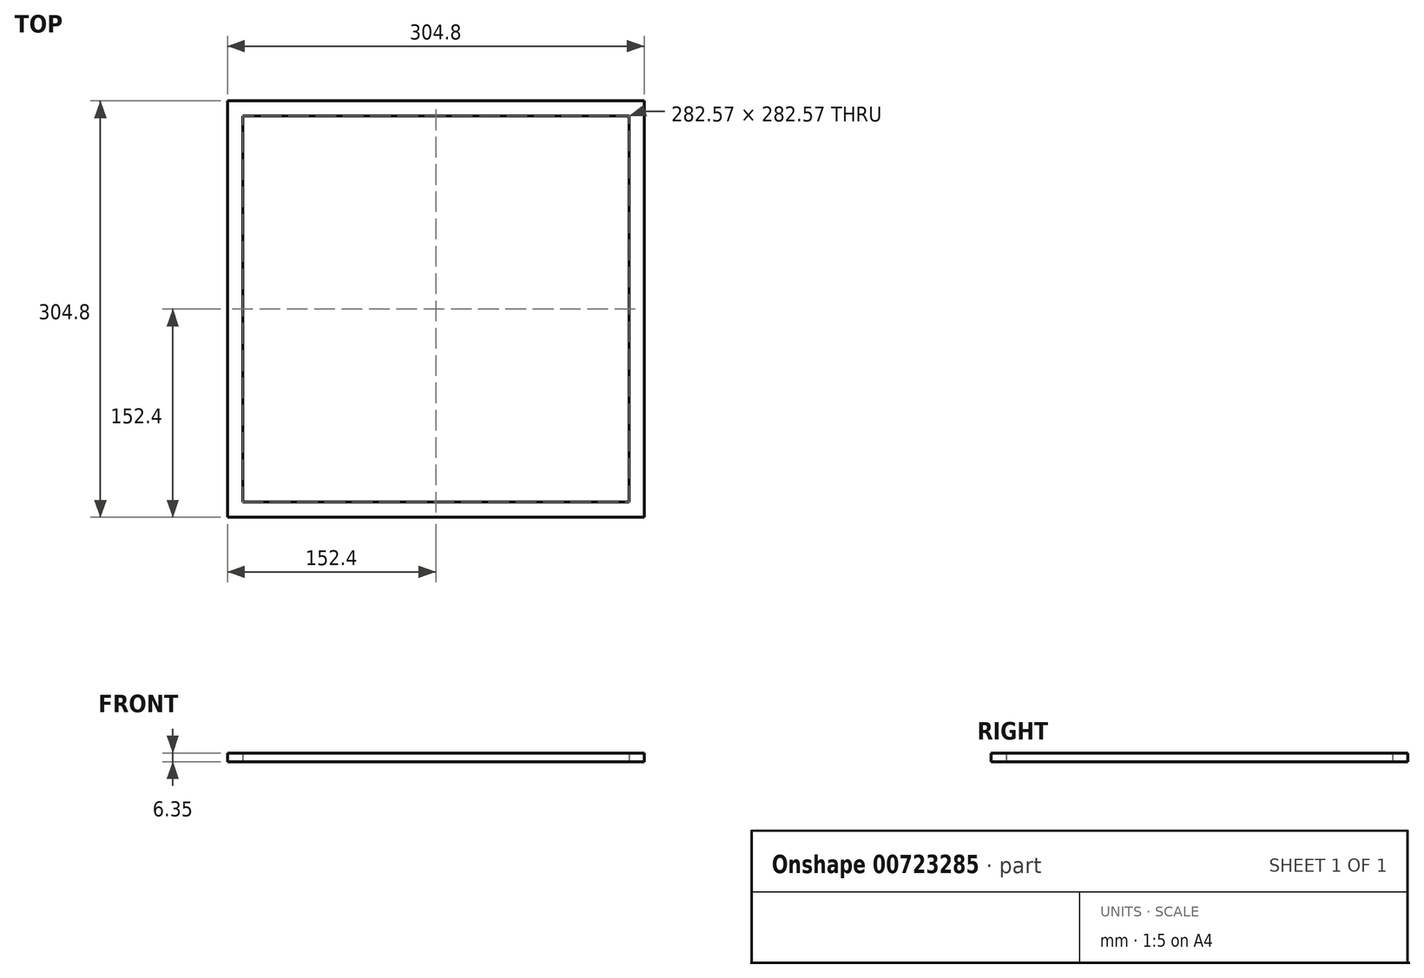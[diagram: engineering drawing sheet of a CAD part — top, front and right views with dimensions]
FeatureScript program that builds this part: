
annotation { "Feature Type Name" : "Feature", "Feature Type Description" : "" }
export const myFeature = defineFeature(function(context is Context, id is Id, definition is map)
    precondition{}
    {
        {
            var Q0;
            Q0=qCreatedBy(makeId("Top.planeOp"),FACE);
            var sketch = newSketch(context, id + "F0", { "sketchPlane" : qUnion([Q0])});
            skLineSegment(sketch, "E0.bottom", {"start": v(141.29, -141.29) * mm, "end": v(-141.29, -141.29) * mm});
            skLineSegment(sketch, "E0.top", {"start": v(141.29, 141.29) * mm, "end": v(-141.29, 141.29) * mm});
            skLineSegment(sketch, "E0.left", {"start": v(141.29, -141.29) * mm, "end": v(141.29, 141.29) * mm});
            skLineSegment(sketch, "E0.right", {"start": v(-141.29, -141.29) * mm, "end": v(-141.29, 141.29) * mm});
            skPoint(sketch, "E0.middle", {"position": v(0, 0) * mm});
            skLineSegment(sketch, "E1.bottom", {"start": v(152.4, -152.4) * mm, "end": v(-152.4, -152.4) * mm});
            skLineSegment(sketch, "E1.top", {"start": v(152.4, 152.4) * mm, "end": v(-152.4, 152.4) * mm});
            skLineSegment(sketch, "E1.left", {"start": v(152.4, -152.4) * mm, "end": v(152.4, 152.4) * mm});
            skLineSegment(sketch, "E1.right", {"start": v(-152.4, -152.4) * mm, "end": v(-152.4, 152.4) * mm});
            skSolve(sketch);
        }
        {
            var Q0;
            Q0=makeQuery(id+"F0.imprint","IMPRINT",FACE,{"disambiguationData":[TD([[makeQuery(id+"F0.imprint","IMPRINT",EDGE,{"derivedFrom":sQuery(id+"F0.wireOp",EDGE,"E0.bottom")}),1.0]])]});
            extrude(context, id + "F1", {"entities" : qUnion([Q0]), "depth" : 6.35 * mm, "offsetDistance" : 25.4 * mm});
        }
    });
